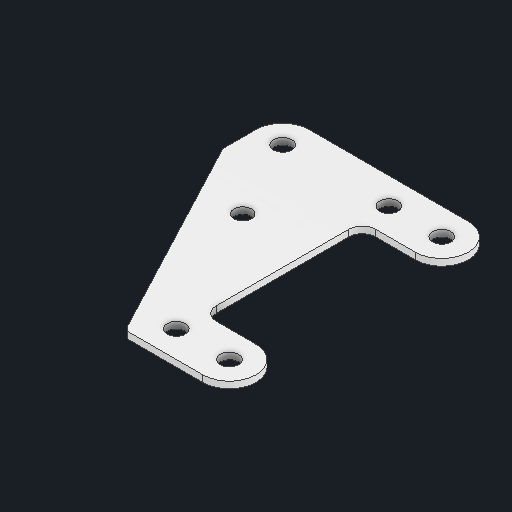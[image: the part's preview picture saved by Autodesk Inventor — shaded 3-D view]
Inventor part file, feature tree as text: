
AUTODESK INVENTOR PART (.ipt)
format: ipt  version: 2025 (Build 290162000, 162)  size: 130,560 bytes
history: native  units: in
note: dims shown in document units (in); Inventor stores cm internally (conversion verified against a paired STEP export)
features: other x5, sketch x1
ambient origin geometry x8: Origin, YZ Plane, XZ Plane, XY Plane, X Axis, Y Axis, Z Axis, Center Point
bodies: Solid1 (feature_tree)
feature tree (6):
  other  "gusset.ipt"
  other  "Blocks"
  other  "main"
  other  "Solid1::gusset.ipt"
  other  "TaggingFeature1"
  sketch  "Sketch1"  dims[d0=0.3937in d3=0.165in]
